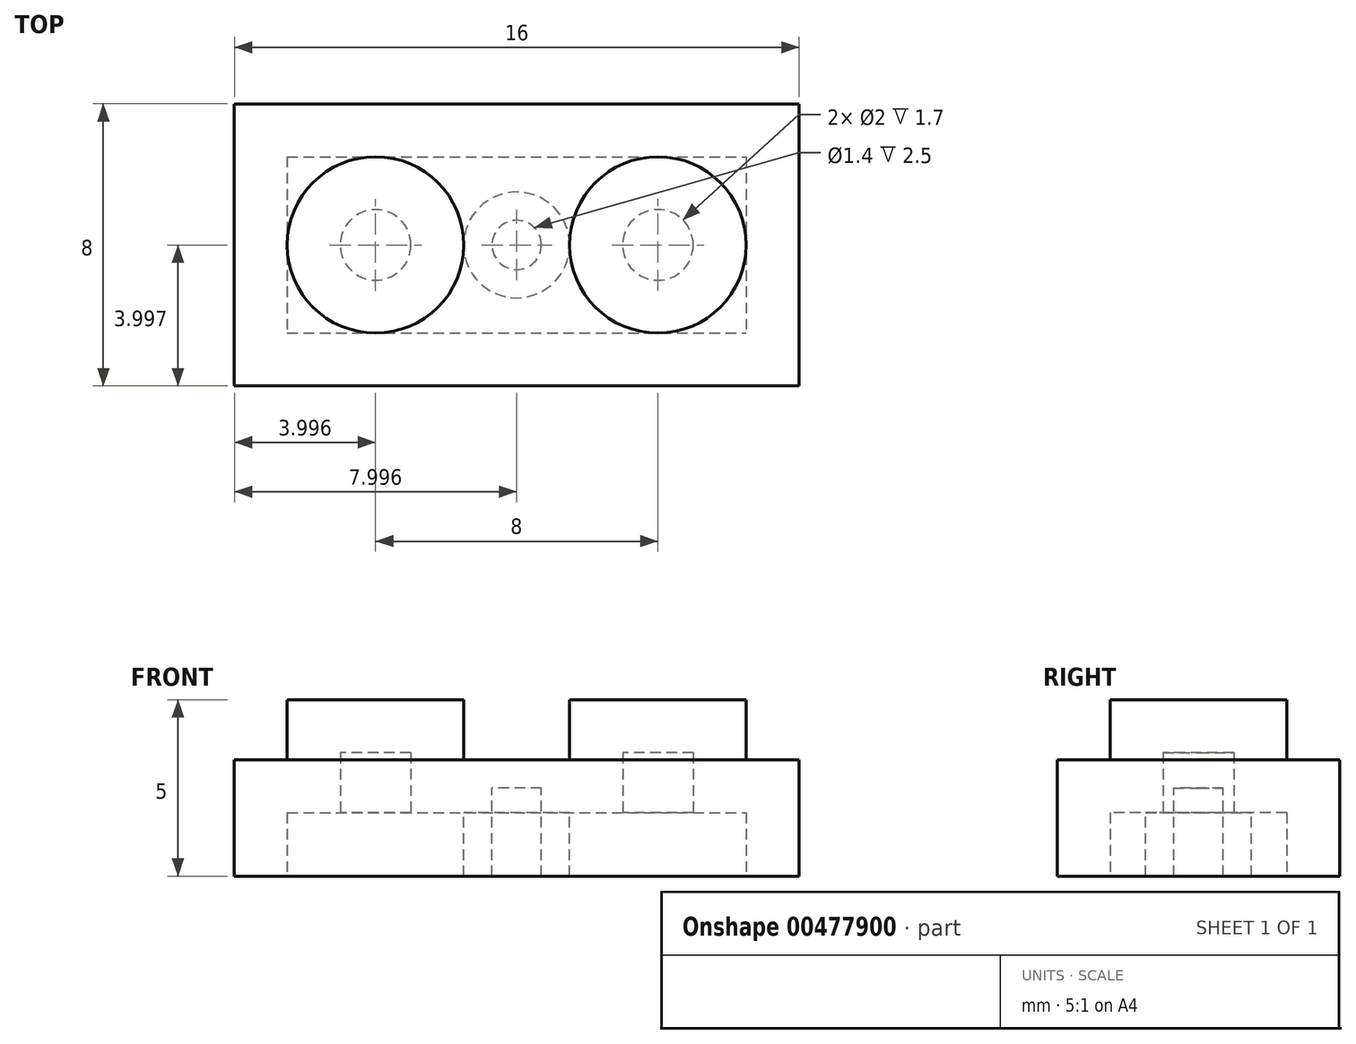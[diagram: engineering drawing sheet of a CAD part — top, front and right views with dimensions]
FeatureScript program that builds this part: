
annotation { "Feature Type Name" : "Feature", "Feature Type Description" : "" }
export const myFeature = defineFeature(function(context is Context, id is Id, definition is map)
    precondition{}
    {
        {
            var Q0;
            Q0=qCreatedBy(makeId("Top.planeOp"),FACE);
            var sketch = newSketch(context, id + "F0", { "sketchPlane" : qUnion([Q0])});
            skLineSegment(sketch, "E0.bottom", {"start": v(-58.33, 39.75) * mm, "end": v(-42.33, 39.75) * mm});
            skLineSegment(sketch, "E0.top", {"start": v(-58.33, 31.75) * mm, "end": v(-42.33, 31.75) * mm});
            skLineSegment(sketch, "E0.left", {"start": v(-58.33, 39.75) * mm, "end": v(-58.33, 31.75) * mm});
            skLineSegment(sketch, "E0.right", {"start": v(-42.33, 39.75) * mm, "end": v(-42.33, 31.75) * mm});
            skSolve(sketch);
        }
        {
            var Q0;
            Q0=makeQuery(id+"F0.imprint","IMPRINT",FACE,{"disambiguationData":[TD([[makeQuery(id+"F0.imprint","IMPRINT",EDGE,{"derivedFrom":sQuery(id+"F0.wireOp",EDGE,"E0.bottom")}),-1.0]])]});
            extrude(context, id + "F1", {"entities" : qUnion([Q0]), "depth" : 3.3 * mm});
        }
        {
            var Q0;
            Q0=makeQuery(id+"F0.imprint","IMPRINT",FACE,{"disambiguationData":[TD([[makeQuery(id+"F0.imprint","IMPRINT",EDGE,{"derivedFrom":sQuery(id+"F0.wireOp",EDGE,"E0.bottom")}),-1.0]])]});
            var sketch = newSketch(context, id + "F2", { "sketchPlane" : qUnion([Q0])});
            skSolve(sketch);
        }
        {
            var Q0;
            Q0=makeQuery(id+"F1.opExtrude","CAP_FACE",FACE,{"disambiguationData":[OSD([sQuery(id+"F0.wireOp",EDGE,"E0.bottom"),sQuery(id+"F0.wireOp",EDGE,"E0.top"),sQuery(id+"F0.wireOp",EDGE,"E0.left"),sQuery(id+"F0.wireOp",EDGE,"E0.right")])],"isStart":false});
            var sketch = newSketch(context, id + "F3", { "sketchPlane" : qUnion([Q0])});
            skCircle(sketch, "E1", {"center": v(-46.33, 35.75) * mm, "radius": 2.5 * mm});
            skCircle(sketch, "E2", {"center": v(-54.33, 35.75) * mm, "radius": 2.5 * mm});
            skSolve(sketch);
        }
        {
            var Q0;
            Q0 = qSketchRegion(id + "F3", true);
            extrude(context, id + "F4", {"entities" : qUnion([Q0]), "operationType" : NewBodyOperationType.ADD, "depth" : 1.7 * mm});
        }
        {
            var Q0;
            Q0=makeQuery(id+"F1.opExtrude","CAP_FACE",FACE,{"disambiguationData":[OSD([sQuery(id+"F0.wireOp",EDGE,"E0.bottom"),sQuery(id+"F0.wireOp",EDGE,"E0.top"),sQuery(id+"F0.wireOp",EDGE,"E0.left"),sQuery(id+"F0.wireOp",EDGE,"E0.right")])],"isStart":false});
            var sketch = newSketch(context, id + "F5", { "sketchPlane" : qUnion([Q0])});
            skPoint(sketch, "E3.endSnap0", {"position": v(-50.33, 31.75) * mm});
            skPoint(sketch, "E3.endSnap1", {"position": v(-58.33, 35.75) * mm});
            skCircle(sketch, "E4", {"center": v(-50.33, 35.75) * mm, "radius": 1.5 * mm});
            skSolve(sketch);
        }
        {
            var Q0;
            Q0=makeQuery(id+"F1.opExtrude","CAP_FACE",FACE,{"disambiguationData":[OSD([sQuery(id+"F0.wireOp",EDGE,"E0.bottom"),sQuery(id+"F0.wireOp",EDGE,"E0.top"),sQuery(id+"F0.wireOp",EDGE,"E0.left"),sQuery(id+"F0.wireOp",EDGE,"E0.right")])],"isStart":true});
            shell(context, id + "F6", {"entities" : qUnion([Q0]), "thickness" : 1.5 * mm});
        }
        {
            var Q0;
            {var subQ0=sQuery(id+"F5.wireOp",EDGE,"E4");var subQ1=makeQuery(id+"F5.imprint","INTERSECT",VERTEX,{"derivedFrom":[makeQuery(id+"F4.opExtrude","CAP_EDGE",EDGE,{"disambiguationData":[OSD([sQuery(id+"F3.wireOp",EDGE,"E1")])],"isStart":true}),subQ0]});Q0=makeQuery(id+"F5.imprint","IMPRINT",FACE,{"disambiguationData":[TD([[makeQuery(id+"F5.imprint","IMPRINT",EDGE,{"disambiguationData":[TD([[subQ1,-1.0]])],"derivedFrom":subQ0}),1.0]])]});}
            extrude(context, id + "F7", {"entities" : qUnion([Q0]), "operationType" : NewBodyOperationType.ADD, "oppositeDirection" : true, "depth" : 3.3 * mm});
        }
        {
            var Q0;
            Q0=makeQuery(id+"F7.opExtrude","CAP_FACE",FACE,{"disambiguationData":[OSD([sQuery(id+"F5.wireOp",EDGE,"E4")])],"isStart":false});
            shell(context, id + "F8", {"entities" : qUnion([Q0]), "thickness" : 0.8 * mm});
        }
    });
